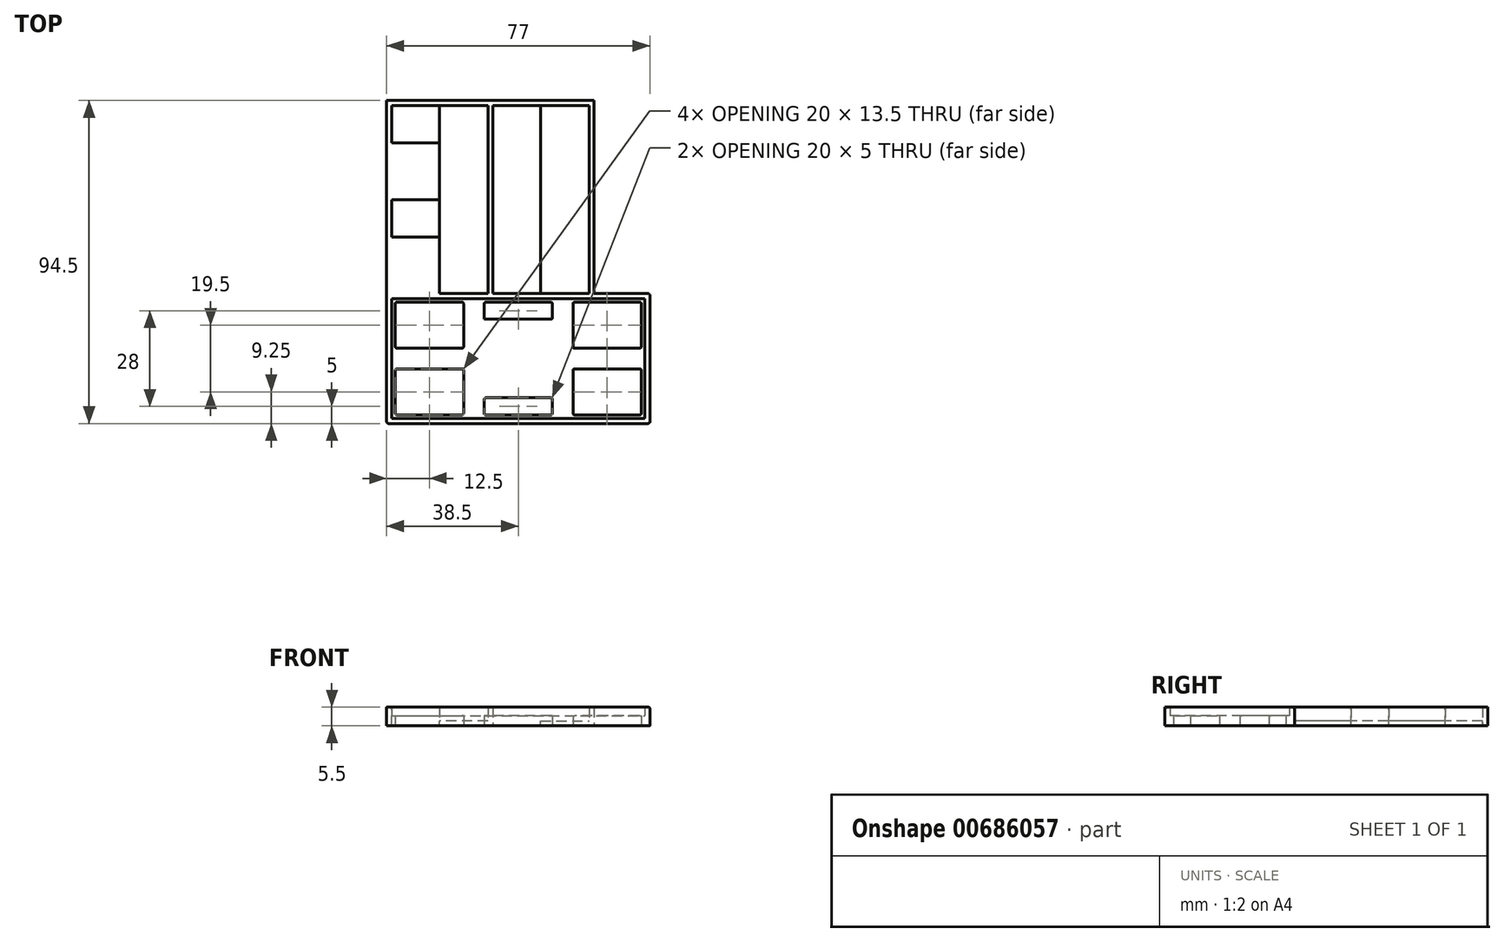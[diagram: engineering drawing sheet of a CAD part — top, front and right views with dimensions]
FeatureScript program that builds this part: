
annotation { "Feature Type Name" : "Feature", "Feature Type Description" : "" }
export const myFeature = defineFeature(function(context is Context, id is Id, definition is map)
    precondition{}
    {
        {
            var Q0;
            Q0=qCreatedBy(makeId("Top.planeOp"),FACE);
            var sketch = newSketch(context, id + "F0", { "sketchPlane" : qUnion([Q0])});
            skLineSegment(sketch, "E0.bottom", {"start": v(-0.75, 29) * mm, "end": v(30.35, 29) * mm});
            skLineSegment(sketch, "E0.top", {"start": v(-0.75, -29) * mm, "end": v(30.35, -29) * mm});
            skLineSegment(sketch, "E0.left", {"start": v(-0.75, 29) * mm, "end": v(-0.75, -29) * mm});
            skLineSegment(sketch, "E0.right", {"start": v(30.35, 29) * mm, "end": v(30.35, -29) * mm});
            skLineSegment(sketch, "E1.0", {"start": v(28.85, 27.5) * mm, "end": v(28.85, -27.5) * mm});
            skLineSegment(sketch, "E1.1", {"start": v(0.75, 27.5) * mm, "end": v(28.85, 27.5) * mm});
            skLineSegment(sketch, "E1.2", {"start": v(0.75, 27.5) * mm, "end": v(0.75, -27.5) * mm});
            skLineSegment(sketch, "E1.3", {"start": v(0.75, -27.5) * mm, "end": v(28.85, -27.5) * mm});
            skPoint(sketch, "E2", {"position": v(28.85, 0) * mm});
            skLineSegment(sketch, "E3", {"start": v(0, -3.8) * mm, "end": v(0, 3.8) * mm, "construction": true});
            skSolve(sketch);
        }
        {
            var Q0;
            Q0=makeQuery(id+"F0.imprint","IMPRINT",FACE,{"disambiguationData":[TD([[makeQuery(id+"F0.imprint","IMPRINT",EDGE,{"derivedFrom":sQuery(id+"F0.wireOp",EDGE,"E0.bottom")}),-1.0]])]});
            extrude(context, id + "F1", {"entities" : qUnion([Q0]), "depth" : 4 * mm, "offsetDistance" : 25 * mm});
        }
        {
            var Q0;
            Q0=makeQuery(id+"F1.opExtrude","SWEPT_BODY",BODY,{"disambiguationData":[OSD([sQuery(id+"F0.wireOp",EDGE,"E0.bottom"),sQuery(id+"F0.wireOp",EDGE,"E0.top"),sQuery(id+"F0.wireOp",EDGE,"E0.left"),sQuery(id+"F0.wireOp",EDGE,"E0.right"),sQuery(id+"F0.wireOp",EDGE,"E1.0"),sQuery(id+"F0.wireOp",EDGE,"E1.1"),sQuery(id+"F0.wireOp",EDGE,"E1.2"),sQuery(id+"F0.wireOp",EDGE,"E1.3"),sQuery(id+"F0.wireOp",EDGE,"u31ZlhcN-V6Ez-q1vK-V0es-5s1ezGJX1rea.bottom"),sQuery(id+"F0.wireOp",EDGE,"u31ZlhcN-V6Ez-q1vK-V0es-5s1ezGJX1rea.left"),sQuery(id+"F0.wireOp",EDGE,"EmW5RWYM-FHgx-2s3S-Z2gW-Hdr9IvvUYMCC.left"),sQuery(id+"F0.wireOp",EDGE,"q6P1yV3w-xWXu-hRzX-XySt-NhQ101tnhMDB.left"),sQuery(id+"F0.wireOp",EDGE,"wc5miMKl-tcxs-jJGE-TOFP-Z4m2yNvy4qyh.bottom"),sQuery(id+"F0.wireOp",EDGE,"wc5miMKl-tcxs-jJGE-TOFP-Z4m2yNvy4qyh.left")])]});
            var Q1;
            Q1=qCreatedBy(makeId("Right.planeOp"),FACE);
            mirror(context, id + "F2", {"operationType" : NewBodyOperationType.ADD, "entities" : qUnion([Q0]), "mirrorPlane" : qUnion([Q1])});
        }
        {
            var Q0;
            Q0=qCreatedBy(makeId("Top.planeOp"),FACE);
            var sketch = newSketch(context, id + "F3", { "sketchPlane" : qUnion([Q0])});
            skLineSegment(sketch, "E4.bottom", {"start": v(-30.35, -29) * mm, "end": v(46.65, -29) * mm});
            skLineSegment(sketch, "E4.top", {"start": v(-30.35, -65.5) * mm, "end": v(46.65, -65.5) * mm});
            skLineSegment(sketch, "E4.left", {"start": v(-30.35, -29) * mm, "end": v(-30.35, -65.5) * mm});
            skLineSegment(sketch, "E4.right", {"start": v(46.65, -29) * mm, "end": v(46.65, -65.5) * mm});
            skLineSegment(sketch, "E5.0", {"start": v(45.15, -29) * mm, "end": v(45.15, -64) * mm});
            skLineSegment(sketch, "E5.1", {"start": v(-28.85, -64) * mm, "end": v(45.15, -64) * mm});
            skLineSegment(sketch, "E5.2", {"start": v(-28.85, -29) * mm, "end": v(-28.85, -64) * mm});
            skLineSegment(sketch, "E6.bottom", {"start": v(46.65, -29) * mm, "end": v(30.35, -29) * mm});
            skLineSegment(sketch, "E6.top", {"start": v(46.65, -27.5) * mm, "end": v(30.35, -27.5) * mm});
            skLineSegment(sketch, "E6.left", {"start": v(46.65, -29) * mm, "end": v(46.65, -27.5) * mm});
            skLineSegment(sketch, "E6.right", {"start": v(30.35, -29) * mm, "end": v(30.35, -27.5) * mm});
            skLineSegment(sketch, "E7.bottom", {"start": v(45.15, -52) * mm, "end": v(46.65, -52) * mm});
            skLineSegment(sketch, "E7.top", {"start": v(45.15, -64) * mm, "end": v(46.65, -64) * mm});
            skLineSegment(sketch, "E7.left", {"start": v(45.15, -52) * mm, "end": v(45.15, -64) * mm});
            skLineSegment(sketch, "E7.right", {"start": v(46.65, -52) * mm, "end": v(46.65, -64) * mm});
            skLineSegment(sketch, "E8", {"start": v(-28.85, -46.5) * mm, "end": v(45.15, -46.5) * mm, "construction": true});
            skLineSegment(sketch, "E9", {"start": v(8.15, -64) * mm, "end": v(8.15, -29) * mm, "construction": true});
            skLineSegment(sketch, "E10.bottom", {"start": v(23.15, -36) * mm, "end": v(-6.85, -36) * mm, "construction": true});
            skLineSegment(sketch, "E10.top", {"start": v(23.15, -57) * mm, "end": v(-6.85, -57) * mm, "construction": true});
            skLineSegment(sketch, "E10.left", {"start": v(23.15, -36) * mm, "end": v(23.15, -57) * mm, "construction": true});
            skLineSegment(sketch, "E10.right", {"start": v(-6.85, -36) * mm, "end": v(-6.85, -57) * mm, "construction": true});
            skPoint(sketch, "E10.middle", {"position": v(8.15, -46.5) * mm});
            skLineSegment(sketch, "E11.bottom", {"start": v(-27.85, -30) * mm, "end": v(-7.85, -30) * mm});
            skLineSegment(sketch, "E11.top", {"start": v(-27.85, -43.5) * mm, "end": v(-7.85, -43.5) * mm});
            skLineSegment(sketch, "E11.left", {"start": v(-27.85, -30) * mm, "end": v(-27.85, -43.5) * mm});
            skLineSegment(sketch, "E11.right", {"start": v(-7.85, -30) * mm, "end": v(-7.85, -43.5) * mm});
            skLineSegment(sketch, "E12.bottom", {"start": v(-1.85, -30) * mm, "end": v(8.15, -30) * mm});
            skLineSegment(sketch, "E12.top", {"start": v(-1.85, -35) * mm, "end": v(8.15, -35) * mm});
            skLineSegment(sketch, "E12.left", {"start": v(-1.85, -30) * mm, "end": v(-1.85, -35) * mm});
            skLineSegment(sketch, "E12.right", {"start": v(8.15, -30) * mm, "end": v(8.15, -35) * mm});
            skLineSegment(sketch, "E13.MirrorCS", {"start": v(18.15, -35) * mm, "end": v(8.15, -35) * mm});
            skLineSegment(sketch, "E14.MirrorCS", {"start": v(18.15, -30) * mm, "end": v(18.15, -35) * mm});
            skLineSegment(sketch, "E15.MirrorCS", {"start": v(18.15, -30) * mm, "end": v(8.15, -30) * mm});
            skLineSegment(sketch, "E16.MirrorCS", {"start": v(24.15, -30) * mm, "end": v(24.15, -43.5) * mm});
            skLineSegment(sketch, "E17.MirrorCS", {"start": v(44.15, -30) * mm, "end": v(24.15, -30) * mm});
            skLineSegment(sketch, "E18.MirrorCS", {"start": v(44.15, -30) * mm, "end": v(44.15, -43.5) * mm});
            skLineSegment(sketch, "E19.MirrorCS", {"start": v(44.15, -43.5) * mm, "end": v(24.15, -43.5) * mm});
            skLineSegment(sketch, "E20.MirrorCS", {"start": v(-27.85, -49.5) * mm, "end": v(-7.85, -49.5) * mm});
            skLineSegment(sketch, "E21.MirrorCS", {"start": v(-7.85, -63) * mm, "end": v(-7.85, -49.5) * mm});
            skLineSegment(sketch, "E22.MirrorCS", {"start": v(-27.85, -63) * mm, "end": v(-7.85, -63) * mm});
            skLineSegment(sketch, "E23.MirrorCS", {"start": v(-27.85, -63) * mm, "end": v(-27.85, -49.5) * mm});
            skLineSegment(sketch, "E24.MirrorCS", {"start": v(-1.85, -63) * mm, "end": v(-1.85, -58) * mm});
            skLineSegment(sketch, "E25.MirrorCS", {"start": v(-1.85, -63) * mm, "end": v(8.15, -63) * mm});
            skLineSegment(sketch, "E26.MirrorCS", {"start": v(-1.85, -58) * mm, "end": v(8.15, -58) * mm});
            skLineSegment(sketch, "E27.MirrorCS", {"start": v(18.15, -58) * mm, "end": v(8.15, -58) * mm});
            skLineSegment(sketch, "E28.MirrorCS", {"start": v(18.15, -63) * mm, "end": v(8.15, -63) * mm});
            skLineSegment(sketch, "E29.MirrorCS", {"start": v(18.15, -63) * mm, "end": v(18.15, -58) * mm});
            skLineSegment(sketch, "E30.MirrorCS", {"start": v(44.15, -63) * mm, "end": v(24.15, -63) * mm});
            skLineSegment(sketch, "E31.MirrorCS", {"start": v(24.15, -63) * mm, "end": v(24.15, -49.5) * mm});
            skLineSegment(sketch, "E32.MirrorCS", {"start": v(44.15, -49.5) * mm, "end": v(24.15, -49.5) * mm});
            skLineSegment(sketch, "E33.MirrorCS", {"start": v(44.15, -63) * mm, "end": v(44.15, -49.5) * mm});
            skSolve(sketch);
        }
        {
            var Q0;
            {var subQ1=sQuery(id+"F3.wireOp",EDGE,"E4.top");Q0=makeQuery(id+"F3.imprint","IMPRINT",FACE,{"disambiguationData":[TD([[makeQuery(id+"F3.imprint","IMPRINT",EDGE,{"derivedFrom":subQ1}),1.0]])]});}
            var Q1;
            {var subQ4=sQuery(id+"F3.wireOp",EDGE,"E5.0");Q1=makeQuery(id+"F3.imprint","IMPRINT",FACE,{"disambiguationData":[TD([[makeQuery(id+"F3.imprint","IMPRINT",EDGE,{"derivedFrom":subQ4}),1.0]])]});}
            var Q2;
            Q2=makeQuery(id+"F3.imprint","IMPRINT",FACE,{"disambiguationData":[TD([[makeQuery(id+"F3.imprint","IMPRINT",EDGE,{"derivedFrom":sQuery(id+"F3.wireOp",EDGE,"E6.top")}),1.0]])]});
            var Q3;
            {var subQ0=sQuery(id+"F0.wireOp",EDGE,"wc5miMKl-tcxs-jJGE-TOFP-Z4m2yNvy4qyh.left");var subQ1=sQuery(id+"F0.wireOp",EDGE,"EmW5RWYM-FHgx-2s3S-Z2gW-Hdr9IvvUYMCC.left");var subQ2=sQuery(id+"F0.wireOp",EDGE,"E1.0");var subQ3=sQuery(id+"F0.wireOp",EDGE,"E0.right");var subQ4=sQuery(id+"F0.wireOp",EDGE,"E0.left");var subQ5=sQuery(id+"F0.wireOp",EDGE,"E0.top");var subQ6=sQuery(id+"F0.wireOp",EDGE,"q6P1yV3w-xWXu-hRzX-XySt-NhQ101tnhMDB.left");var subQ7=sQuery(id+"F0.wireOp",EDGE,"u31ZlhcN-V6Ez-q1vK-V0es-5s1ezGJX1rea.left");var subQ8=sQuery(id+"F0.wireOp",EDGE,"E1.2");var subQ9=sQuery(id+"F0.wireOp",EDGE,"wc5miMKl-tcxs-jJGE-TOFP-Z4m2yNvy4qyh.bottom");var subQ10=sQuery(id+"F0.wireOp",EDGE,"E1.3");var subQ11=makeQuery(id+"F3wA3jW3quZKjiT_1.boolean.opBoolean","SPLIT",FACE,{"disambiguationData":[TD([makeQuery(id+"F1.opExtrude","SWEPT_FACE",FACE,{"disambiguationData":[OSD([subQ5])]}),makeQuery(id+"F1.opExtrude","SWEPT_FACE",FACE,{"disambiguationData":[OSD([subQ4])]}),makeQuery(id+"F1.opExtrude","SWEPT_FACE",FACE,{"disambiguationData":[OSD([subQ3])]}),makeQuery(id+"F1.opExtrude","SWEPT_FACE",FACE,{"disambiguationData":[OSD([subQ2,subQ1,subQ0])]}),makeQuery(id+"F1.opExtrude","SWEPT_FACE",FACE,{"disambiguationData":[OSD([subQ8,subQ7,subQ6])]}),makeQuery(id+"F1.opExtrude","SWEPT_FACE",FACE,{"disambiguationData":[OSD([subQ10,subQ9])]}),makeQuery(id+"F3wA3jW3quZKjiT_1.opExtrude","SWEPT_FACE",FACE,{"disambiguationData":[OSD([sQuery(id+"FWevqYpBtpJXgHf_1.wireOp",EDGE,"10ofWLOM-Fa8D-Ud0r-HqvO-9BuwmLjWM0FR")])]})])],"derivedFrom":makeQuery(id+"F1.opExtrude","CAP_FACE",FACE,{"disambiguationData":[OSD([sQuery(id+"F0.wireOp",EDGE,"E0.bottom"),subQ5,subQ4,subQ3,subQ2,sQuery(id+"F0.wireOp",EDGE,"E1.1"),subQ8,subQ10,sQuery(id+"F0.wireOp",EDGE,"u31ZlhcN-V6Ez-q1vK-V0es-5s1ezGJX1rea.bottom"),subQ7,subQ1,subQ6,subQ9,subQ0])],"isStart":false})});Q3=makeQuery(id+"F2.boolean.opBoolean","MERGE",FACE,{"derivedFrom":[subQ11,makeQuery(id+"F2.opPattern","COPY",FACE,{"derivedFrom":subQ11,"instanceName":"1"})]});}
            extrude(context, id + "F4", {"entities" : qUnion([Q0, Q1, Q2]), "operationType" : NewBodyOperationType.ADD, "endBound" : BoundingType.UP_TO_SURFACE, "depth" : 25 * mm, "endBoundEntityFace" : qUnion([Q3]), "offsetDistance" : 25 * mm});
        }
        {
            var Q0;
            {var subQ1=sQuery(id+"F3.wireOp",EDGE,"E5.0");Q0=makeQuery(id+"F3.imprint","IMPRINT",FACE,{"disambiguationData":[TD([[makeQuery(id+"F3.imprint","IMPRINT",EDGE,{"derivedFrom":subQ1}),-1.0]])]});}
            var Q1;
            Q1=makeQuery(id+"F3.imprint","IMPRINT",FACE,{"disambiguationData":[TD([[makeQuery(id+"F3.imprint","IMPRINT",EDGE,{"derivedFrom":sQuery(id+"F3.wireOp",EDGE,"E7.bottom")}),-1.0]])]});
            extrude(context, id + "F5", {"entities" : qUnion([Q0, Q1]), "operationType" : NewBodyOperationType.ADD, "depth" : 1.5 * mm, "offsetDistance" : 25 * mm});
        }
        {
            var Q0;
            Q0=makeQuery(id+"F4.opExtrude","SWEPT_EDGE",EDGE,{"disambiguationData":[OSD([sQuery(id+"F3.wireOp",EDGE,"E6.top"),sQuery(id+"F3.wireOp",EDGE,"E6.left")])]});
            var Q1;
            Q1=makeQuery(id+"F4.opExtrude","CAP_EDGE",EDGE,{"disambiguationData":[OSD([sQuery(id+"F3.wireOp",EDGE,"E7.bottom")])],"isStart":false});
            var Q2;
            Q2=makeQuery(id+"F4.opExtrude","CAP_EDGE",EDGE,{"disambiguationData":[OSD([sQuery(id+"F3.wireOp",EDGE,"E4.right")])],"isStart":false});
            var Q3;
            Q3=makeQuery(id+"F4.opExtrude","SWEPT_EDGE",EDGE,{"disambiguationData":[OSD([sQuery(id+"F3.wireOp",EDGE,"E4.top"),sQuery(id+"F3.wireOp",EDGE,"E4.right")])]});
            var Q4;
            Q4=makeQuery(id+"F4.opExtrude","SWEPT_EDGE",EDGE,{"disambiguationData":[OSD([sQuery(id+"F3.wireOp",EDGE,"E4.right"),sQuery(id+"F3.wireOp",EDGE,"E7.bottom"),sQuery(id+"F3.wireOp",EDGE,"E7.right")])]});
            var Q5;
            Q5=makeQuery(id+"F4.opExtrude","SWEPT_EDGE",EDGE,{"disambiguationData":[OSD([sQuery(id+"F3.wireOp",EDGE,"E4.right"),sQuery(id+"F3.wireOp",EDGE,"E7.top"),sQuery(id+"F3.wireOp",EDGE,"E7.right")])]});
            var Q6;
            Q6=makeQuery(id+"F4.opExtrude","SWEPT_EDGE",EDGE,{"disambiguationData":[OSD([sQuery(id+"F3.wireOp",EDGE,"E4.top"),sQuery(id+"F3.wireOp",EDGE,"E4.left")])]});
            var Q7;
            Q7=makeQuery(id+"F5.opExtrude","SWEPT_EDGE",EDGE,{"disambiguationData":[OSD([sQuery(id+"F3.wireOp",EDGE,"E11.bottom"),sQuery(id+"F3.wireOp",EDGE,"E11.left")])]});
            var Q8;
            Q8=makeQuery(id+"F5.opExtrude","SWEPT_EDGE",EDGE,{"disambiguationData":[OSD([sQuery(id+"F3.wireOp",EDGE,"E11.bottom"),sQuery(id+"F3.wireOp",EDGE,"E11.right")])]});
            var Q9;
            Q9=makeQuery(id+"F5.opExtrude","SWEPT_EDGE",EDGE,{"disambiguationData":[OSD([sQuery(id+"F3.wireOp",EDGE,"E12.bottom"),sQuery(id+"F3.wireOp",EDGE,"E12.left")])]});
            var Q10;
            Q10=makeQuery(id+"F5.opExtrude","SWEPT_EDGE",EDGE,{"disambiguationData":[OSD([sQuery(id+"F3.wireOp",EDGE,"E14.MirrorCS"),sQuery(id+"F3.wireOp",EDGE,"E15.MirrorCS")])]});
            var Q11;
            Q11=makeQuery(id+"F5.opExtrude","SWEPT_EDGE",EDGE,{"disambiguationData":[OSD([sQuery(id+"F3.wireOp",EDGE,"E16.MirrorCS"),sQuery(id+"F3.wireOp",EDGE,"E17.MirrorCS")])]});
            var Q12;
            Q12=makeQuery(id+"F5.opExtrude","SWEPT_EDGE",EDGE,{"disambiguationData":[OSD([sQuery(id+"F3.wireOp",EDGE,"E17.MirrorCS"),sQuery(id+"F3.wireOp",EDGE,"E18.MirrorCS")])]});
            var Q13;
            Q13=makeQuery(id+"F5.opExtrude","SWEPT_EDGE",EDGE,{"disambiguationData":[OSD([sQuery(id+"F3.wireOp",EDGE,"E16.MirrorCS"),sQuery(id+"F3.wireOp",EDGE,"E19.MirrorCS")])]});
            var Q14;
            Q14=makeQuery(id+"F5.opExtrude","SWEPT_EDGE",EDGE,{"disambiguationData":[OSD([sQuery(id+"F3.wireOp",EDGE,"E18.MirrorCS"),sQuery(id+"F3.wireOp",EDGE,"E19.MirrorCS")])]});
            var Q15;
            Q15=makeQuery(id+"F5.opExtrude","SWEPT_EDGE",EDGE,{"disambiguationData":[OSD([sQuery(id+"F3.wireOp",EDGE,"E13.MirrorCS"),sQuery(id+"F3.wireOp",EDGE,"E14.MirrorCS")])]});
            var Q16;
            Q16=makeQuery(id+"F5.opExtrude","SWEPT_EDGE",EDGE,{"disambiguationData":[OSD([sQuery(id+"F3.wireOp",EDGE,"E11.top"),sQuery(id+"F3.wireOp",EDGE,"E11.right")])]});
            var Q17;
            Q17=makeQuery(id+"F5.opExtrude","SWEPT_EDGE",EDGE,{"disambiguationData":[OSD([sQuery(id+"F3.wireOp",EDGE,"E21.MirrorCS"),sQuery(id+"F3.wireOp",EDGE,"E22.MirrorCS")])]});
            var Q18;
            Q18=makeQuery(id+"F5.opExtrude","SWEPT_EDGE",EDGE,{"disambiguationData":[OSD([sQuery(id+"F3.wireOp",EDGE,"E28.MirrorCS"),sQuery(id+"F3.wireOp",EDGE,"E29.MirrorCS")])]});
            var Q19;
            Q19=makeQuery(id+"F5.opExtrude","SWEPT_EDGE",EDGE,{"disambiguationData":[OSD([sQuery(id+"F3.wireOp",EDGE,"E30.MirrorCS"),sQuery(id+"F3.wireOp",EDGE,"E33.MirrorCS")])]});
            var Q20;
            Q20=makeQuery(id+"F5.opExtrude","SWEPT_EDGE",EDGE,{"disambiguationData":[OSD([sQuery(id+"F3.wireOp",EDGE,"E20.MirrorCS"),sQuery(id+"F3.wireOp",EDGE,"E23.MirrorCS")])]});
            var Q21;
            Q21=makeQuery(id+"F5.opExtrude","SWEPT_EDGE",EDGE,{"disambiguationData":[OSD([sQuery(id+"F3.wireOp",EDGE,"E24.MirrorCS"),sQuery(id+"F3.wireOp",EDGE,"E26.MirrorCS")])]});
            var Q22;
            Q22=makeQuery(id+"F5.opExtrude","SWEPT_EDGE",EDGE,{"disambiguationData":[OSD([sQuery(id+"F3.wireOp",EDGE,"E31.MirrorCS"),sQuery(id+"F3.wireOp",EDGE,"E32.MirrorCS")])]});
            var Q23;
            Q23=makeQuery(id+"F5.opExtrude","SWEPT_EDGE",EDGE,{"disambiguationData":[OSD([sQuery(id+"F3.wireOp",EDGE,"E27.MirrorCS"),sQuery(id+"F3.wireOp",EDGE,"E29.MirrorCS")])]});
            var Q24;
            Q24=makeQuery(id+"F5.opExtrude","SWEPT_EDGE",EDGE,{"disambiguationData":[OSD([sQuery(id+"F3.wireOp",EDGE,"E32.MirrorCS"),sQuery(id+"F3.wireOp",EDGE,"E33.MirrorCS")])]});
            var Q25;
            Q25=makeQuery(id+"F5.opExtrude","SWEPT_EDGE",EDGE,{"disambiguationData":[OSD([sQuery(id+"F3.wireOp",EDGE,"E20.MirrorCS"),sQuery(id+"F3.wireOp",EDGE,"E21.MirrorCS")])]});
            var Q26;
            Q26=makeQuery(id+"F5.opExtrude","SWEPT_EDGE",EDGE,{"disambiguationData":[OSD([sQuery(id+"F3.wireOp",EDGE,"E30.MirrorCS"),sQuery(id+"F3.wireOp",EDGE,"E31.MirrorCS")])]});
            var Q27;
            Q27=makeQuery(id+"F5.opExtrude","SWEPT_EDGE",EDGE,{"disambiguationData":[OSD([sQuery(id+"F3.wireOp",EDGE,"E24.MirrorCS"),sQuery(id+"F3.wireOp",EDGE,"E25.MirrorCS")])]});
            var Q28;
            Q28=makeQuery(id+"F5.opExtrude","SWEPT_EDGE",EDGE,{"disambiguationData":[OSD([sQuery(id+"F3.wireOp",EDGE,"E22.MirrorCS"),sQuery(id+"F3.wireOp",EDGE,"E23.MirrorCS")])]});
            var Q29;
            Q29=makeQuery(id+"F5.opExtrude","SWEPT_EDGE",EDGE,{"disambiguationData":[OSD([sQuery(id+"F3.wireOp",EDGE,"E11.top"),sQuery(id+"F3.wireOp",EDGE,"E11.left")])]});
            fillet(context, id + "F6", {"entities" : qUnion([Q0, Q1, Q2, Q3, Q4, Q5, Q6, Q7, Q8, Q9, Q10, Q11, Q12, Q13, Q14, Q15, Q16, Q17, Q18, Q19, Q20, Q21, Q22, Q23, Q24, Q25, Q26, Q27, Q28, Q29]), "radius" : 0.5 * mm, "tangentPropagation" : true, "allowEdgeOverflow" : false});
        }
        {
            var Q0;
            Q0=qCreatedBy(makeId("Top.planeOp"),FACE);
            var sketch = newSketch(context, id + "F7", { "sketchPlane" : qUnion([Q0])});
            skLineSegment(sketch, "E34.bottom", {"start": v(-0.75, 27.5) * mm, "end": v(-14.9, 27.5) * mm});
            skLineSegment(sketch, "E34.top", {"start": v(-0.75, -27.62) * mm, "end": v(-14.9, -27.62) * mm});
            skLineSegment(sketch, "E34.left", {"start": v(-0.75, 27.5) * mm, "end": v(-0.75, -27.62) * mm});
            skLineSegment(sketch, "E34.right", {"start": v(-14.9, 27.5) * mm, "end": v(-14.9, -27.62) * mm});
            skLineSegment(sketch, "E35.bottom", {"start": v(28.85, 27.5) * mm, "end": v(14.7, 27.5) * mm});
            skLineSegment(sketch, "E35.top", {"start": v(28.85, -27.58) * mm, "end": v(14.7, -27.58) * mm});
            skLineSegment(sketch, "E35.left", {"start": v(28.85, 27.5) * mm, "end": v(28.85, -27.58) * mm});
            skLineSegment(sketch, "E35.right", {"start": v(14.7, 27.5) * mm, "end": v(14.7, -27.58) * mm});
            skLineSegment(sketch, "E36.bottom", {"start": v(14.7, -27.58) * mm, "end": v(-28.85, -27.58) * mm});
            skLineSegment(sketch, "E36.top", {"start": v(14.7, -10.97) * mm, "end": v(-28.85, -10.97) * mm});
            skLineSegment(sketch, "E36.left", {"start": v(14.7, -27.58) * mm, "end": v(14.7, -10.97) * mm});
            skLineSegment(sketch, "E36.right", {"start": v(-28.85, -27.58) * mm, "end": v(-28.85, -10.97) * mm});
            skLineSegment(sketch, "E37.bottom", {"start": v(14.7, 0) * mm, "end": v(-28.85, 0) * mm});
            skLineSegment(sketch, "E37.top", {"start": v(14.7, 16.6) * mm, "end": v(-28.85, 16.6) * mm});
            skLineSegment(sketch, "E37.left", {"start": v(14.7, 0) * mm, "end": v(14.7, 16.6) * mm});
            skLineSegment(sketch, "E37.right", {"start": v(-28.85, 0) * mm, "end": v(-28.85, 16.6) * mm});
            skSolve(sketch);
        }
        {
            var Q0;
            {var subQ0=sQuery(id+"F3.wireOp",EDGE,"E7.top");var subQ1=sQuery(id+"F3.wireOp",EDGE,"E7.bottom");var subQ2=sQuery(id+"F3.wireOp",EDGE,"E6.bottom");var subQ3=sQuery(id+"F3.wireOp",EDGE,"E5.2");var subQ4=sQuery(id+"F3.wireOp",EDGE,"E5.1");var subQ5=sQuery(id+"F3.wireOp",EDGE,"E5.0");var subQ6=sQuery(id+"F3.wireOp",EDGE,"E4.bottom");var subQ7=sQuery(id+"F3.wireOp",EDGE,"E4.right");var subQ8=sQuery(id+"F0.wireOp",EDGE,"wc5miMKl-tcxs-jJGE-TOFP-Z4m2yNvy4qyh.left");var subQ9=sQuery(id+"F0.wireOp",EDGE,"wc5miMKl-tcxs-jJGE-TOFP-Z4m2yNvy4qyh.bottom");var subQ10=sQuery(id+"F0.wireOp",EDGE,"q6P1yV3w-xWXu-hRzX-XySt-NhQ101tnhMDB.left");var subQ11=sQuery(id+"F0.wireOp",EDGE,"EmW5RWYM-FHgx-2s3S-Z2gW-Hdr9IvvUYMCC.left");var subQ12=sQuery(id+"F0.wireOp",EDGE,"u31ZlhcN-V6Ez-q1vK-V0es-5s1ezGJX1rea.left");var subQ13=sQuery(id+"F0.wireOp",EDGE,"u31ZlhcN-V6Ez-q1vK-V0es-5s1ezGJX1rea.bottom");var subQ14=makeQuery(id+"FKj87NXetBHEBJO_1.boolean.opBoolean","MERGE",FACE,{"derivedFrom":[makeQuery(id+"F1.opExtrude","CAP_FACE",FACE,{"disambiguationData":[OSD([sQuery(id+"F0.wireOp",EDGE,"E0.bottom"),sQuery(id+"F0.wireOp",EDGE,"E0.top"),sQuery(id+"F0.wireOp",EDGE,"E0.left"),sQuery(id+"F0.wireOp",EDGE,"E0.right"),sQuery(id+"F0.wireOp",EDGE,"E1.0"),sQuery(id+"F0.wireOp",EDGE,"E1.1"),sQuery(id+"F0.wireOp",EDGE,"E1.2"),sQuery(id+"F0.wireOp",EDGE,"E1.3"),subQ13,subQ12,subQ11,subQ10,subQ9,subQ8])],"isStart":true}),makeQuery(id+"FKj87NXetBHEBJO_1.opExtrude","CAP_FACE",FACE,{"disambiguationData":[OSD([subQ13,sQuery(id+"F0.wireOp",EDGE,"u31ZlhcN-V6Ez-q1vK-V0es-5s1ezGJX1rea.top"),subQ12,sQuery(id+"F0.wireOp",EDGE,"u31ZlhcN-V6Ez-q1vK-V0es-5s1ezGJX1rea.right")])],"isStart":true}),makeQuery(id+"FKj87NXetBHEBJO_1.opExtrude","CAP_FACE",FACE,{"disambiguationData":[OSD([sQuery(id+"F0.wireOp",EDGE,"EmW5RWYM-FHgx-2s3S-Z2gW-Hdr9IvvUYMCC.bottom"),sQuery(id+"F0.wireOp",EDGE,"EmW5RWYM-FHgx-2s3S-Z2gW-Hdr9IvvUYMCC.top"),subQ11,sQuery(id+"F0.wireOp",EDGE,"EmW5RWYM-FHgx-2s3S-Z2gW-Hdr9IvvUYMCC.right")])],"isStart":true}),makeQuery(id+"FKj87NXetBHEBJO_1.opExtrude","CAP_FACE",FACE,{"disambiguationData":[OSD([sQuery(id+"F0.wireOp",EDGE,"q6P1yV3w-xWXu-hRzX-XySt-NhQ101tnhMDB.bottom"),sQuery(id+"F0.wireOp",EDGE,"q6P1yV3w-xWXu-hRzX-XySt-NhQ101tnhMDB.top"),subQ10,sQuery(id+"F0.wireOp",EDGE,"q6P1yV3w-xWXu-hRzX-XySt-NhQ101tnhMDB.right")])],"isStart":true}),makeQuery(id+"FKj87NXetBHEBJO_1.opExtrude","CAP_FACE",FACE,{"disambiguationData":[OSD([subQ9,sQuery(id+"F0.wireOp",EDGE,"wc5miMKl-tcxs-jJGE-TOFP-Z4m2yNvy4qyh.top"),subQ8,sQuery(id+"F0.wireOp",EDGE,"wc5miMKl-tcxs-jJGE-TOFP-Z4m2yNvy4qyh.right")])],"isStart":true})]});Q0=makeQuery(id+"F5.boolean.opBoolean","MERGE",FACE,{"derivedFrom":[makeQuery(id+"F4.boolean.opBoolean","MERGE",FACE,{"derivedFrom":[makeQuery(id+"F2.boolean.opBoolean","MERGE",FACE,{"derivedFrom":[subQ14,makeQuery(id+"F2.opPattern","COPY",FACE,{"derivedFrom":subQ14,"instanceName":"1"})]}),makeQuery(id+"F4.opExtrude","CAP_FACE",FACE,{"disambiguationData":[OSD([subQ6,sQuery(id+"F3.wireOp",EDGE,"E4.top"),sQuery(id+"F3.wireOp",EDGE,"E4.left"),subQ7,subQ4,subQ3,subQ0])],"isStart":true}),makeQuery(id+"F4.opExtrude","CAP_FACE",FACE,{"disambiguationData":[OSD([subQ7,subQ5,subQ2,sQuery(id+"F3.wireOp",EDGE,"E6.top"),sQuery(id+"F3.wireOp",EDGE,"E6.left"),sQuery(id+"F3.wireOp",EDGE,"E6.right"),subQ1])],"isStart":true})]}),makeQuery(id+"F5.opExtrude","CAP_FACE",FACE,{"disambiguationData":[OSD([subQ6,subQ5,subQ4,subQ3,subQ2,subQ1,subQ0,sQuery(id+"F3.wireOp",EDGE,"E7.right"),sQuery(id+"F3.wireOp",EDGE,"E11.bottom"),sQuery(id+"F3.wireOp",EDGE,"E11.top"),sQuery(id+"F3.wireOp",EDGE,"E11.left"),sQuery(id+"F3.wireOp",EDGE,"E11.right"),sQuery(id+"F3.wireOp",EDGE,"E12.bottom"),sQuery(id+"F3.wireOp",EDGE,"E12.top"),sQuery(id+"F3.wireOp",EDGE,"E12.left"),sQuery(id+"F3.wireOp",EDGE,"E13.MirrorCS"),sQuery(id+"F3.wireOp",EDGE,"E14.MirrorCS"),sQuery(id+"F3.wireOp",EDGE,"E15.MirrorCS"),sQuery(id+"F3.wireOp",EDGE,"E16.MirrorCS"),sQuery(id+"F3.wireOp",EDGE,"E17.MirrorCS"),sQuery(id+"F3.wireOp",EDGE,"E18.MirrorCS"),sQuery(id+"F3.wireOp",EDGE,"E19.MirrorCS"),sQuery(id+"F3.wireOp",EDGE,"E20.MirrorCS"),sQuery(id+"F3.wireOp",EDGE,"E21.MirrorCS"),sQuery(id+"F3.wireOp",EDGE,"E22.MirrorCS"),sQuery(id+"F3.wireOp",EDGE,"E23.MirrorCS"),sQuery(id+"F3.wireOp",EDGE,"E24.MirrorCS"),sQuery(id+"F3.wireOp",EDGE,"E25.MirrorCS"),sQuery(id+"F3.wireOp",EDGE,"E26.MirrorCS"),sQuery(id+"F3.wireOp",EDGE,"E27.MirrorCS"),sQuery(id+"F3.wireOp",EDGE,"E28.MirrorCS"),sQuery(id+"F3.wireOp",EDGE,"E29.MirrorCS"),sQuery(id+"F3.wireOp",EDGE,"E30.MirrorCS"),sQuery(id+"F3.wireOp",EDGE,"E31.MirrorCS"),sQuery(id+"F3.wireOp",EDGE,"E32.MirrorCS"),sQuery(id+"F3.wireOp",EDGE,"E33.MirrorCS")])],"isStart":true})]});}
            var Q1;
            {var subQ5=sQuery(id+"F7.wireOp",EDGE,"E37.right");Q1=makeQuery(id+"F7.imprint","IMPRINT",FACE,{"disambiguationData":[TD([[makeQuery(id+"F7.imprint","IMPRINT",EDGE,{"derivedFrom":subQ5}),-1.0]])]});}
            var Q2;
            {var subQ0=sQuery(id+"F7.wireOp",EDGE,"E34.bottom");Q2=makeQuery(id+"F7.imprint","IMPRINT",FACE,{"disambiguationData":[TD([[makeQuery(id+"F7.imprint","IMPRINT",EDGE,{"derivedFrom":subQ0}),1.0]])]});}
            var Q3;
            {var subQ0=sQuery(id+"F7.wireOp",EDGE,"E37.top");var subQ1=sQuery(id+"F7.wireOp",EDGE,"E34.left");var subQ2=makeQuery(id+"F7.imprint","INTERSECT",VERTEX,{"derivedFrom":[subQ1,subQ0]});Q3=makeQuery(id+"F7.imprint","IMPRINT",FACE,{"disambiguationData":[TD([[makeQuery(id+"F7.imprint","IMPRINT",EDGE,{"disambiguationData":[TD([[subQ2,-1.0]])],"derivedFrom":subQ1}),-1.0]])]});}
            var Q4;
            {var subQ1=sQuery(id+"F7.wireOp",EDGE,"E35.bottom");Q4=makeQuery(id+"F7.imprint","IMPRINT",FACE,{"disambiguationData":[TD([[makeQuery(id+"F7.imprint","IMPRINT",EDGE,{"derivedFrom":subQ1}),1.0]])]});}
            var Q5;
            {var subQ5=sQuery(id+"F7.wireOp",EDGE,"E37.left");Q5=makeQuery(id+"F7.imprint","IMPRINT",FACE,{"disambiguationData":[TD([[makeQuery(id+"F7.imprint","IMPRINT",EDGE,{"derivedFrom":subQ5}),1.0]])]});}
            var Q6;
            {var subQ5=sQuery(id+"F7.wireOp",EDGE,"E36.left");Q6=makeQuery(id+"F7.imprint","IMPRINT",FACE,{"disambiguationData":[TD([[makeQuery(id+"F7.imprint","IMPRINT",EDGE,{"derivedFrom":subQ5}),1.0]])]});}
            var Q7;
            {var subQ0=sQuery(id+"F7.wireOp",EDGE,"E36.bottom");var subQ1=sQuery(id+"F7.wireOp",EDGE,"E34.left");var subQ2=makeQuery(id+"F7.imprint","INTERSECT",VERTEX,{"derivedFrom":[subQ1,subQ0]});Q7=makeQuery(id+"F7.imprint","IMPRINT",FACE,{"disambiguationData":[TD([[makeQuery(id+"F7.imprint","IMPRINT",EDGE,{"disambiguationData":[TD([[subQ2,1.0]])],"derivedFrom":subQ1}),-1.0]])]});}
            var Q8;
            {var subQ5=sQuery(id+"F7.wireOp",EDGE,"E36.right");Q8=makeQuery(id+"F7.imprint","IMPRINT",FACE,{"disambiguationData":[TD([[makeQuery(id+"F7.imprint","IMPRINT",EDGE,{"derivedFrom":subQ5}),-1.0]])]});}
            var Q9;
            {var subQ0=sQuery(id+"F7.wireOp",EDGE,"E37.bottom");var subQ1=sQuery(id+"F7.wireOp",EDGE,"E34.left");var subQ2=makeQuery(id+"F7.imprint","INTERSECT",VERTEX,{"derivedFrom":[subQ1,subQ0]});Q9=makeQuery(id+"F7.imprint","IMPRINT",FACE,{"disambiguationData":[TD([[makeQuery(id+"F7.imprint","IMPRINT",EDGE,{"disambiguationData":[TD([[subQ2,-1.0]])],"derivedFrom":subQ1}),-1.0]])]});}
            extrude(context, id + "F8", {"entities" : qUnion([Q0, Q1, Q2, Q3, Q4, Q5, Q6, Q7, Q8, Q9]), "operationType" : NewBodyOperationType.ADD, "depth" : 1.5 * mm, "offsetDistance" : 25 * mm});
        }
        {
            var Q0;
            {var subQ5=sQuery(id+"F7.wireOp",EDGE,"E37.right");Q0=makeQuery(id+"F7.imprint","IMPRINT",FACE,{"disambiguationData":[TD([[makeQuery(id+"F7.imprint","IMPRINT",EDGE,{"derivedFrom":subQ5}),-1.0]])]});}
            var Q1;
            {var subQ5=sQuery(id+"F7.wireOp",EDGE,"E36.right");Q1=makeQuery(id+"F7.imprint","IMPRINT",FACE,{"disambiguationData":[TD([[makeQuery(id+"F7.imprint","IMPRINT",EDGE,{"derivedFrom":subQ5}),-1.0]])]});}
            var Q2;
            {var subQ5=sQuery(id+"F7.wireOp",EDGE,"E36.left");Q2=makeQuery(id+"F7.imprint","IMPRINT",FACE,{"disambiguationData":[TD([[makeQuery(id+"F7.imprint","IMPRINT",EDGE,{"derivedFrom":subQ5}),1.0]])]});}
            var Q3;
            {var subQ5=sQuery(id+"F7.wireOp",EDGE,"E37.left");Q3=makeQuery(id+"F7.imprint","IMPRINT",FACE,{"disambiguationData":[TD([[makeQuery(id+"F7.imprint","IMPRINT",EDGE,{"derivedFrom":subQ5}),1.0]])]});}
            var Q4;
            {var subQ0=sQuery(id+"F0.wireOp",EDGE,"E1.3");var subQ1=sQuery(id+"F0.wireOp",EDGE,"E1.2");var subQ2=sQuery(id+"F0.wireOp",EDGE,"E1.1");var subQ3=sQuery(id+"F0.wireOp",EDGE,"E1.0");var subQ4=sQuery(id+"F0.wireOp",EDGE,"E0.right");var subQ5=sQuery(id+"F0.wireOp",EDGE,"E0.left");var subQ6=sQuery(id+"F0.wireOp",EDGE,"E0.top");var subQ7=sQuery(id+"F0.wireOp",EDGE,"E0.bottom");var subQ8=makeQuery(id+"F1.opExtrude","CAP_FACE",FACE,{"disambiguationData":[OSD([subQ7,subQ6,subQ5,subQ4,subQ3,subQ2,subQ1,subQ0])],"isStart":false});Q4=makeQuery(id+"F4.boolean.opBoolean","MERGE",FACE,{"derivedFrom":[makeQuery(id+"F2.boolean.opBoolean","MERGE",FACE,{"derivedFrom":[subQ8,makeQuery(id+"F2.opPattern","COPY",FACE,{"derivedFrom":subQ8,"instanceName":"1"})]}),makeQuery(id+"F4.opExtrude","CAP_FACE",FACE,{"disambiguationData":[OSD([subQ7,subQ6,subQ5,subQ4,subQ3,subQ2,subQ1,subQ0]),OD(0.0)],"isStart":false}),makeQuery(id+"F4.opExtrude","CAP_FACE",FACE,{"disambiguationData":[OSD([subQ7,subQ6,subQ5,subQ4,subQ3,subQ2,subQ1,subQ0]),OD(1.0)],"isStart":false})]});}
            extrude(context, id + "F9", {"entities" : qUnion([Q0, Q1, Q2, Q3]), "operationType" : NewBodyOperationType.ADD, "endBound" : BoundingType.UP_TO_SURFACE, "depth" : 25 * mm, "endBoundEntityFace" : qUnion([Q4]), "offsetDistance" : 25 * mm});
        }
    });
